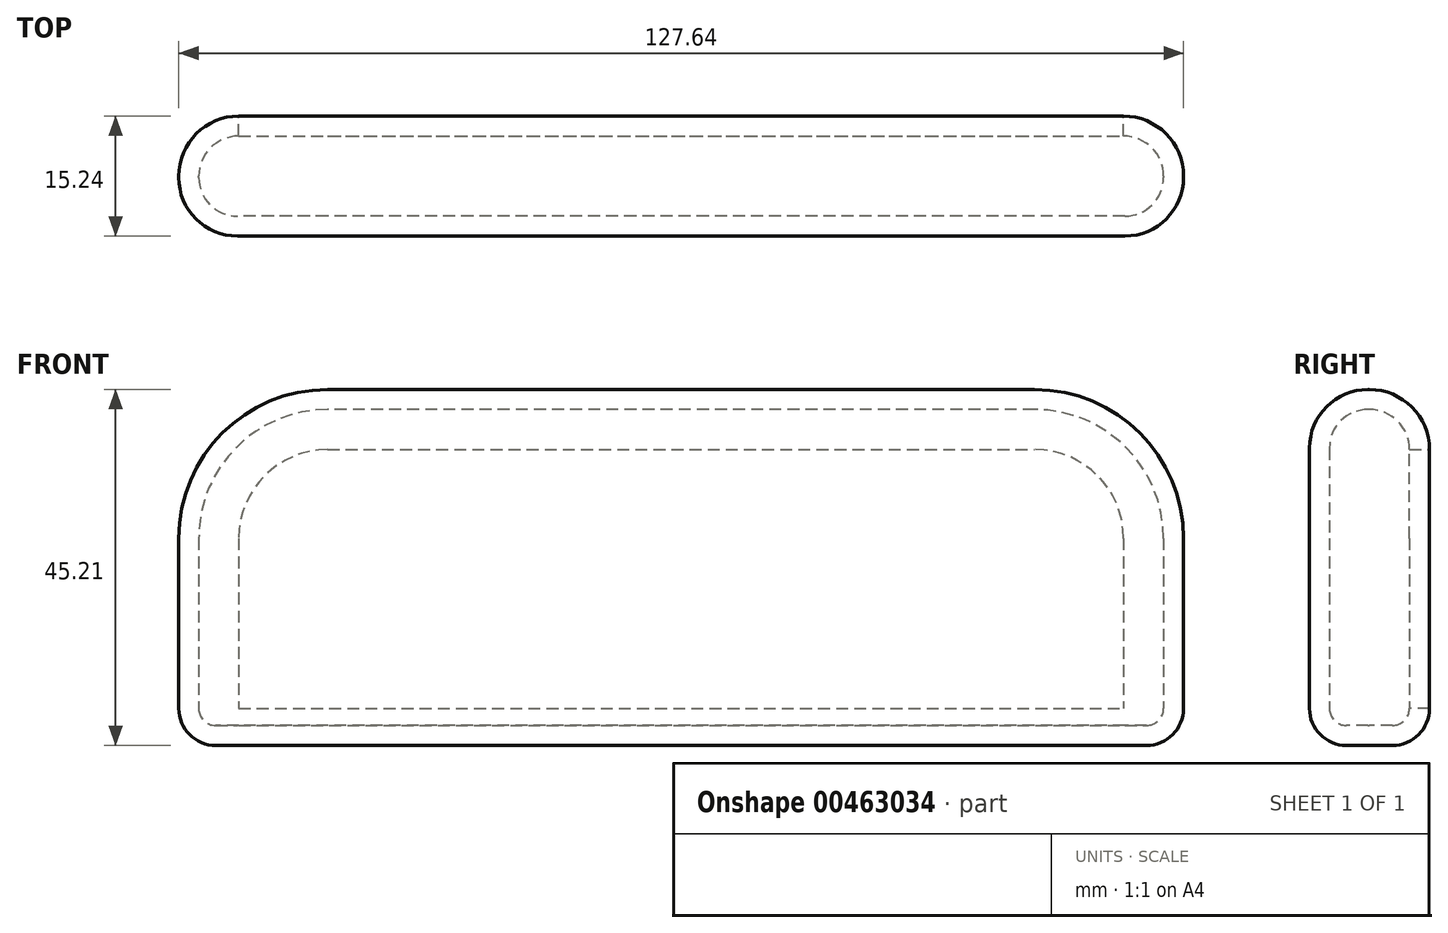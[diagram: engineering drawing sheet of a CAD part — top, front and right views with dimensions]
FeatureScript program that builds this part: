
annotation { "Feature Type Name" : "Feature", "Feature Type Description" : "" }
export const myFeature = defineFeature(function(context is Context, id is Id, definition is map)
    precondition{}
    {
        {
            var Q0;
            Q0=qCreatedBy(makeId("Top.planeOp"),FACE);
            var sketch = newSketch(context, id + "F0", { "sketchPlane" : qUnion([Q0])});
            skLineSegment(sketch, "E0", {"start": v(-60.6, 49.45) * mm, "end": v(61.95, 49.45) * mm});
            skLineSegment(sketch, "E1", {"start": v(61.95, 49.45) * mm, "end": v(61.95, 39.29) * mm});
            skLineSegment(sketch, "E2", {"start": v(61.95, 39.29) * mm, "end": v(-60.6, 39.29) * mm});
            skLineSegment(sketch, "E3", {"start": v(-60.6, 39.29) * mm, "end": v(-60.6, 49.45) * mm});
            skSolve(sketch);
        }
        {
            var Q0;
            Q0 = qSketchRegion(id + "F0", true);
            extrude(context, id + "F1", {"entities" : qUnion([Q0]), "depth" : 40.13 * mm});
        }
        {
            var Q0;
            Q0=makeQuery(id+"F1.opExtrude","SWEPT_EDGE",EDGE,{"disambiguationData":[OSD([sQuery(id+"F0.wireOp",EDGE,"E1"),sQuery(id+"F0.wireOp",EDGE,"E2")])]});
            var Q1;
            Q1=makeQuery(id+"F1.opExtrude","CAP_EDGE",EDGE,{"disambiguationData":[OSD([sQuery(id+"F0.wireOp",EDGE,"E2")])],"isStart":false});
            var Q2;
            Q2=makeQuery(id+"F1.opExtrude","SWEPT_EDGE",EDGE,{"disambiguationData":[OSD([sQuery(id+"F0.wireOp",EDGE,"E2"),sQuery(id+"F0.wireOp",EDGE,"E3")])]});
            fillet(context, id + "F2", {"entities" : qUnion([Q0, Q1, Q2]), "radius" : 4.9 * mm, "allowEdgeOverflow" : false});
        }
        {
            var Q0;
            Q0=makeQuery(id+"F1.opExtrude","CAP_EDGE",EDGE,{"disambiguationData":[OSD([sQuery(id+"F0.wireOp",EDGE,"E3")])],"isStart":true});
            var Q1;
            Q1=makeQuery(id+"F1.opExtrude","CAP_FACE",FACE,{"disambiguationData":[OSD([sQuery(id+"F0.wireOp",EDGE,"E0"),sQuery(id+"F0.wireOp",EDGE,"E1"),sQuery(id+"F0.wireOp",EDGE,"E2"),sQuery(id+"F0.wireOp",EDGE,"E3")])],"isStart":true});
            fillet(context, id + "F3", {"entities" : qUnion([Q0, Q1]), "radius" : 2.15 * mm, "tangentPropagation" : true, "allowEdgeOverflow" : false});
        }
        {
            var Q0;
            Q0=makeQuery(id+"F1.opExtrude","CAP_EDGE",EDGE,{"disambiguationData":[OSD([sQuery(id+"F0.wireOp",EDGE,"E3")])],"isStart":false});
            var Q1;
            {var subQ0=sQuery(id+"F0.wireOp",EDGE,"E2");Q1=makeQuery(id+"F2.opFillet","BLEND_EDGE",EDGE,{"blendedFrom":[makeQuery(id+"F1.opExtrude","SWEPT_EDGE",EDGE,{"disambiguationData":[OSD([subQ0,sQuery(id+"F0.wireOp",EDGE,"E3")])]}),makeQuery(id+"F1.opExtrude","CAP_EDGE",EDGE,{"disambiguationData":[OSD([subQ0])],"isStart":false})],"blendedInto":[]});}
            var Q2;
            {var subQ0=sQuery(id+"F0.wireOp",EDGE,"E2");Q2=makeQuery(id+"F2.opFillet","BLEND_EDGE",EDGE,{"blendedFrom":[makeQuery(id+"F1.opExtrude","SWEPT_EDGE",EDGE,{"disambiguationData":[OSD([sQuery(id+"F0.wireOp",EDGE,"E1"),subQ0])]}),makeQuery(id+"F1.opExtrude","CAP_EDGE",EDGE,{"disambiguationData":[OSD([subQ0])],"isStart":false})],"blendedInto":[]});}
            var Q3;
            Q3=makeQuery(id+"F1.opExtrude","CAP_EDGE",EDGE,{"disambiguationData":[OSD([sQuery(id+"F0.wireOp",EDGE,"E1")])],"isStart":false});
            fillet(context, id + "F4", {"entities" : qUnion([Q0, Q1, Q2, Q3]), "radius" : 16.37 * mm, "tangentPropagation" : true, "allowEdgeOverflow" : false});
        }
        {
            var Q0;
            Q0=makeQuery(id+"F1.opExtrude","SWEPT_EDGE",EDGE,{"disambiguationData":[OSD([sQuery(id+"F0.wireOp",EDGE,"E0"),sQuery(id+"F0.wireOp",EDGE,"E3")])]});
            var Q1;
            Q1=makeQuery(id+"F4.opFillet","BLEND_EDGE",EDGE,{"blendedFrom":[makeQuery(id+"F1.opExtrude","CAP_EDGE",EDGE,{"disambiguationData":[OSD([sQuery(id+"F0.wireOp",EDGE,"E3")])],"isStart":false}),makeQuery(id+"F1.opExtrude","SWEPT_FACE",FACE,{"disambiguationData":[OSD([sQuery(id+"F0.wireOp",EDGE,"E0")])]})],"blendedInto":[makeQuery(id+"F1.opExtrude","SWEPT_FACE",FACE,{"disambiguationData":[OSD([sQuery(id+"F0.wireOp",EDGE,"E0")])]})]});
            var Q2;
            Q2=makeQuery(id+"F1.opExtrude","CAP_EDGE",EDGE,{"disambiguationData":[OSD([sQuery(id+"F0.wireOp",EDGE,"E0")])],"isStart":false});
            var Q3;
            Q3=makeQuery(id+"F4.opFillet","BLEND_EDGE",EDGE,{"blendedFrom":[makeQuery(id+"F1.opExtrude","CAP_EDGE",EDGE,{"disambiguationData":[OSD([sQuery(id+"F0.wireOp",EDGE,"E1")])],"isStart":false}),makeQuery(id+"F1.opExtrude","SWEPT_FACE",FACE,{"disambiguationData":[OSD([sQuery(id+"F0.wireOp",EDGE,"E0")])]})],"blendedInto":[makeQuery(id+"F1.opExtrude","SWEPT_FACE",FACE,{"disambiguationData":[OSD([sQuery(id+"F0.wireOp",EDGE,"E0")])]})]});
            var Q4;
            Q4=makeQuery(id+"F1.opExtrude","SWEPT_EDGE",EDGE,{"disambiguationData":[OSD([sQuery(id+"F0.wireOp",EDGE,"E0"),sQuery(id+"F0.wireOp",EDGE,"E1")])]});
            var Q5;
            Q5=makeQuery(id+"F3.opFillet","BLEND_EDGE",EDGE,{"blendedFrom":[makeQuery(id+"F1.opExtrude","CAP_EDGE",EDGE,{"disambiguationData":[OSD([sQuery(id+"F0.wireOp",EDGE,"E0")])],"isStart":true}),makeQuery(id+"F1.opExtrude","CAP_EDGE",EDGE,{"disambiguationData":[OSD([sQuery(id+"F0.wireOp",EDGE,"E1")])],"isStart":true})],"blendedInto":[]});
            var Q6;
            Q6=makeQuery(id+"F1.opExtrude","SWEPT_FACE",FACE,{"disambiguationData":[OSD([sQuery(id+"F0.wireOp",EDGE,"E0")])]});
            var Q7;
            Q7=makeQuery(id+"F1.opExtrude","CAP_FACE",FACE,{"disambiguationData":[OSD([sQuery(id+"F0.wireOp",EDGE,"E0"),sQuery(id+"F0.wireOp",EDGE,"E1"),sQuery(id+"F0.wireOp",EDGE,"E2"),sQuery(id+"F0.wireOp",EDGE,"E3")])],"isStart":false});
            var Q8;
            Q8=makeQuery(id+"F3.opFillet","BLEND_EDGE",EDGE,{"blendedFrom":[makeQuery(id+"F1.opExtrude","CAP_EDGE",EDGE,{"disambiguationData":[OSD([sQuery(id+"F0.wireOp",EDGE,"E0")])],"isStart":true}),makeQuery(id+"F1.opExtrude","CAP_EDGE",EDGE,{"disambiguationData":[OSD([sQuery(id+"F0.wireOp",EDGE,"E3")])],"isStart":true})],"blendedInto":[]});
            fillet(context, id + "F5", {"entities" : qUnion([Q0, Q1, Q2, Q3, Q4, Q5, Q6, Q7, Q8]), "radius" : 5.08 * mm, "tangentPropagation" : true, "allowEdgeOverflow" : false});
        }
        {
            var Q0;
            Q0=makeQuery(id+"F1.opExtrude","SWEPT_FACE",FACE,{"disambiguationData":[OSD([sQuery(id+"F0.wireOp",EDGE,"E0")])]});
            shell(context, id + "F6", {"entities" : qUnion([Q0]), "thickness" : 2.54 * mm, "oppositeDirection" : true});
        }
    });
